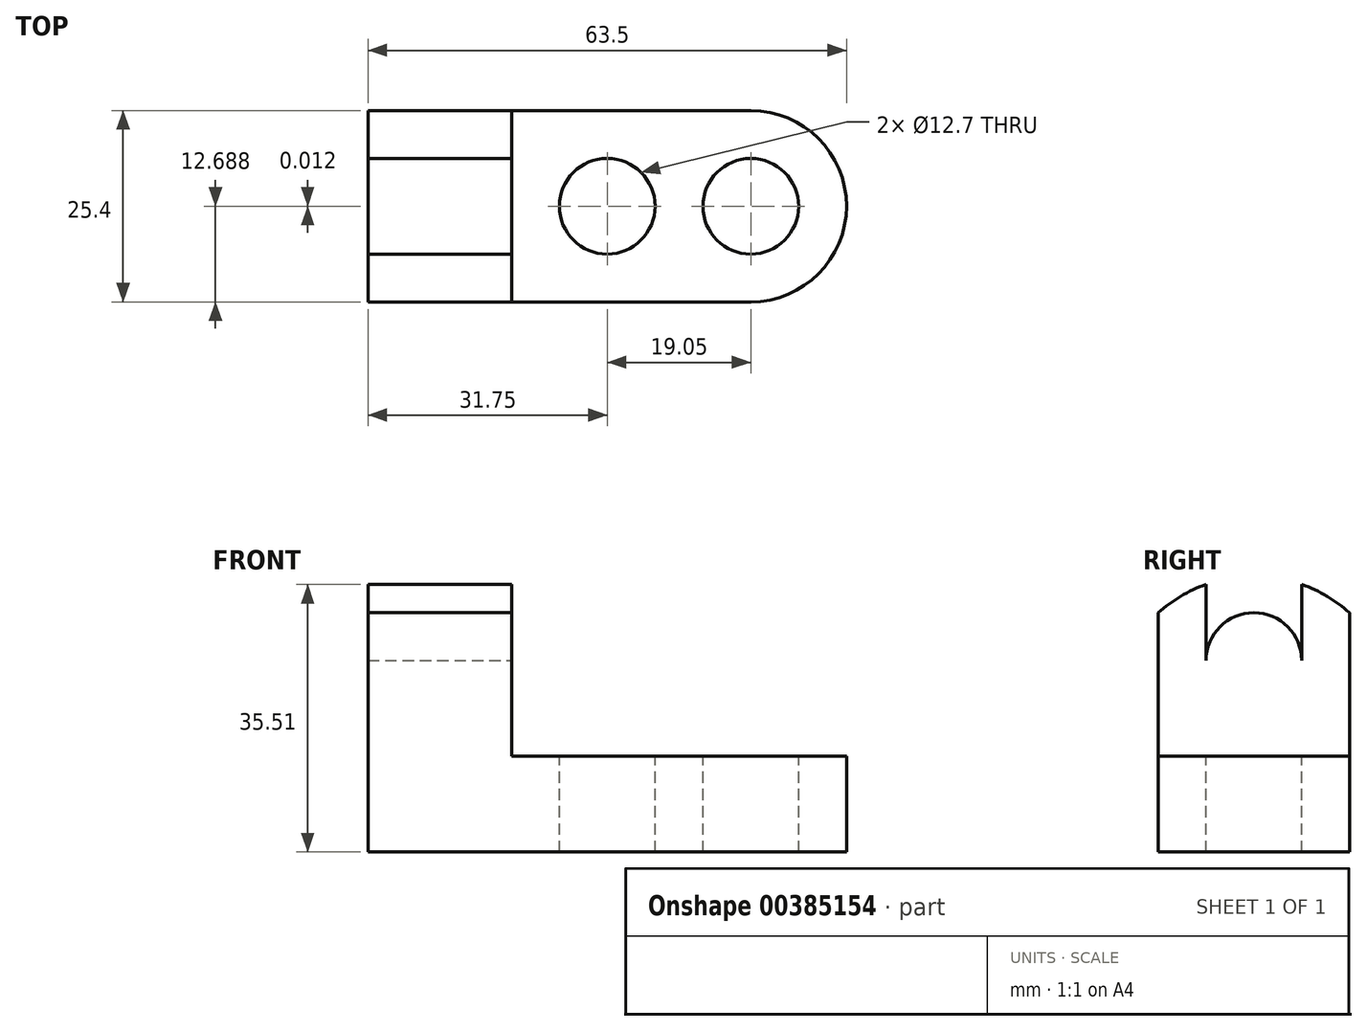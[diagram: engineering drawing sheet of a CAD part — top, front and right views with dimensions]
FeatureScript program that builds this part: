
annotation { "Feature Type Name" : "Feature", "Feature Type Description" : "" }
export const myFeature = defineFeature(function(context is Context, id is Id, definition is map)
    precondition{}
    {
        {
            var Q0;
            Q0=qCreatedBy(makeId("Front.planeOp"),FACE);
            var sketch = newSketch(context, id + "F0", { "sketchPlane" : qUnion([Q0])});
            skLineSegment(sketch, "E0", {"start": v(0, 0) * mm, "end": v(0, 38.1) * mm});
            skLineSegment(sketch, "E1", {"start": v(0, 38.1) * mm, "end": v(19.05, 38.1) * mm});
            skLineSegment(sketch, "E2", {"start": v(19.05, 38.1) * mm, "end": v(19.05, 12.7) * mm});
            skLineSegment(sketch, "E3", {"start": v(19.05, 12.7) * mm, "end": v(63.5, 12.7) * mm});
            skLineSegment(sketch, "E4", {"start": v(63.5, 12.7) * mm, "end": v(63.5, 0) * mm});
            skLineSegment(sketch, "E5", {"start": v(63.5, 0) * mm, "end": v(0, 0) * mm});
            skSolve(sketch);
        }
        {
            var Q0;
            Q0 = qSketchRegion(id + "F0", true);
            extrude(context, id + "F1", {"entities" : qUnion([Q0]), "depth" : 25.4 * mm});
        }
        {
            var Q0;
            Q0=makeQuery(id+"F1.opExtrude","SWEPT_FACE",FACE,{"disambiguationData":[OSD([sQuery(id+"F0.wireOp",EDGE,"E3")])]});
            var sketch = newSketch(context, id + "F2", { "sketchPlane" : qUnion([Q0])});
            skCircle(sketch, "E6", {"center": v(31.75, -12.7) * mm, "radius": 6.35 * mm});
            skPoint(sketch, "E6.centerSnap0", {"position": v(19.05, -12.7) * mm});
            skCircle(sketch, "E7", {"center": v(50.8, -12.71) * mm, "radius": 6.35 * mm});
            skSolve(sketch);
        }
        {
            var Q0;
            Q0=makeQuery(id+"F2.imprint","IMPRINT",FACE,{"disambiguationData":[TD([[makeQuery(id+"F2.imprint","IMPRINT",EDGE,{"derivedFrom":sQuery(id+"F2.wireOp",EDGE,"E6")}),1.0]])]});
            var Q1;
            Q1=makeQuery(id+"F2.imprint","IMPRINT",FACE,{"disambiguationData":[TD([[makeQuery(id+"F2.imprint","IMPRINT",EDGE,{"derivedFrom":sQuery(id+"F2.wireOp",EDGE,"E7")}),1.0]])]});
            extrude(context, id + "F3", {"entities" : qUnion([Q0, Q1]), "operationType" : NewBodyOperationType.REMOVE, "oppositeDirection" : true, "depth" : 25.4 * mm});
        }
        {
            var Q0;
            Q0=makeQuery(id+"F1.opExtrude","SWEPT_FACE",FACE,{"disambiguationData":[OSD([sQuery(id+"F0.wireOp",EDGE,"E3")])]});
            var sketch = newSketch(context, id + "F4", { "sketchPlane" : qUnion([Q0])});
            skArc(sketch, "E8", {"start": v(50.8, -25.4) * mm, "mid": v(63.5, -12.7) * mm, "end": v(50.8, 0) * mm});
            skSolve(sketch);
        }
        {
            var Q0;
            {var subQ0=sQuery(id+"F4.wireOp",EDGE,"E8");var subQ1=sQuery(id+"F0.wireOp",EDGE,"E3");var subQ2=makeQuery(id+"F1.opExtrude","CAP_EDGE",EDGE,{"disambiguationData":[OSD([subQ1])],"isStart":false});var subQ3=makeQuery(id+"F4.imprint","INTERSECT",VERTEX,{"derivedFrom":[subQ2,subQ0]});Q0=makeQuery(id+"F4.imprint","IMPRINT",FACE,{"disambiguationData":[TD([[makeQuery(id+"F4.imprint","IMPRINT",EDGE,{"disambiguationData":[TD([[subQ3,-1.0]])],"derivedFrom":subQ0}),-1.0]])]});}
            var Q1;
            {var subQ0=sQuery(id+"F4.wireOp",EDGE,"E8");var subQ1=sQuery(id+"F0.wireOp",EDGE,"E3");var subQ2=makeQuery(id+"F1.opExtrude","CAP_EDGE",EDGE,{"disambiguationData":[OSD([subQ1])],"isStart":true});var subQ3=makeQuery(id+"F4.imprint","INTERSECT",VERTEX,{"derivedFrom":[subQ2,subQ0]});Q1=makeQuery(id+"F4.imprint","IMPRINT",FACE,{"disambiguationData":[TD([[makeQuery(id+"F4.imprint","IMPRINT",EDGE,{"disambiguationData":[TD([[subQ3,1.0]])],"derivedFrom":subQ0}),-1.0]])]});}
            extrude(context, id + "F5", {"entities" : qUnion([Q0, Q1]), "operationType" : NewBodyOperationType.REMOVE, "oppositeDirection" : true, "depth" : 25.4 * mm});
        }
        {
            var Q0;
            Q0=makeQuery(id+"F1.opExtrude","SWEPT_FACE",FACE,{"disambiguationData":[OSD([sQuery(id+"F0.wireOp",EDGE,"E2")])]});
            var sketch = newSketch(context, id + "F6", { "sketchPlane" : qUnion([Q0])});
            skSolve(sketch);
        }
        {
            var Q0;
            {var subQ0=sQuery(id+"F0.wireOp",EDGE,"E2");Q0=makeQuery(id+"F6.imprint","IMPRINT",FACE,{"disambiguationData":[TD([[makeQuery(id+"F6.imprint","IMPRINT",EDGE,{"derivedFrom":makeQuery(id+"F1.opExtrude","CAP_EDGE",EDGE,{"disambiguationData":[OSD([subQ0])],"isStart":true})}),-1.0]])]});}
            var sketch = newSketch(context, id + "F7", { "sketchPlane" : qUnion([Q0])});
            skCircle(sketch, "E9", {"center": v(-12.7, 25.4) * mm, "radius": 6.35 * mm});
            skLineSegment(sketch, "E10", {"start": v(-6.35, 25.4) * mm, "end": v(-6.35, 38.1) * mm});
            skLineSegment(sketch, "E11", {"start": v(-19.05, 25.4) * mm, "end": v(-19.05, 38.1) * mm});
            skSolve(sketch);
        }
        {
            var Q0;
            {var subQ0=sQuery(id+"F7.wireOp",EDGE,"E9");var subQ2=makeQuery(id+"F7.imprint","IMPRINT",VERTEX,{"derivedFrom":subQ0});Q0=makeQuery(id+"F7.imprint","IMPRINT",FACE,{"disambiguationData":[TD([[makeQuery(id+"F7.imprint","IMPRINT",EDGE,{"disambiguationData":[TD([[subQ2,1.0]])],"derivedFrom":subQ0}),1.0]])]});}
            var Q1;
            {var subQ0=sQuery(id+"F7.wireOp",EDGE,"E10");Q1=makeQuery(id+"F7.imprint","IMPRINT",FACE,{"disambiguationData":[TD([[makeQuery(id+"F7.imprint","IMPRINT",EDGE,{"derivedFrom":subQ0}),1.0]])]});}
            extrude(context, id + "F8", {"entities" : qUnion([Q0, Q1]), "operationType" : NewBodyOperationType.REMOVE, "oppositeDirection" : true, "depth" : 25.4 * mm});
        }
        {
            var Q0;
            {var subQ0=sQuery(id+"F0.wireOp",EDGE,"E2");Q0=makeQuery(id+"F6.imprint","IMPRINT",FACE,{"disambiguationData":[TD([[makeQuery(id+"F6.imprint","IMPRINT",EDGE,{"derivedFrom":makeQuery(id+"F1.opExtrude","CAP_EDGE",EDGE,{"disambiguationData":[OSD([subQ0])],"isStart":true})}),-1.0]])]});}
            var sketch = newSketch(context, id + "F9", { "sketchPlane" : qUnion([Q0])});
            skArc(sketch, "E12", {"start": v(0, 31.75) * mm, "mid": v(-12.7, 36.6) * mm, "end": v(-25.4, 31.75) * mm});
            skSolve(sketch);
        }
        {
            var Q0;
            {var subQ0=sQuery(id+"F9.wireOp",EDGE,"E12");Q0=makeQuery(id+"F9.imprint","IMPRINT",FACE,{"disambiguationData":[TD([[makeQuery(id+"F9.imprint","IMPRINT",EDGE,{"derivedFrom":subQ0}),-1.0]])]});}
            extrude(context, id + "F10", {"entities" : qUnion([Q0]), "operationType" : NewBodyOperationType.REMOVE, "oppositeDirection" : true, "depth" : 25.4 * mm});
        }
    });
